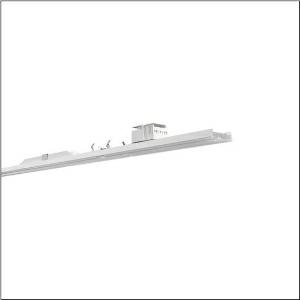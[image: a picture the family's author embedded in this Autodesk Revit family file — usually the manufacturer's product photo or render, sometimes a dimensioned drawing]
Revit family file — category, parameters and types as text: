
# Revit family: licross_r__11_recessed_extreme_mo_51tl11dn49xfe_ba7a
name_source: partatom
category: Lighting Fixtures
units: mm (PartAtom-declared; Revit-internal decimal feet)

## family parameters
Cut with Voids When Loaded = No
Host = Face
Light Source = No
Part Type = Normal
Room Calculation Point = No
Round Connector Dimension = Use Diameter
Shared = No

## types (1)
- --- (1 x LED, 9030 lm, 55.4 W, 4000K)
    Apparent Load = 55 VA
    CIE Flux Codes = 89 96 99 100 100
    Color Rendering = 80
    Color Temperature = 4000K
    Default Elevation = 1800 mm
    Description = Licross® 11 Recessed extreme MOluminaire insert, length: 1.500mm, width: 66mm, height: 67mm, LED rated luminous flux: 9.030lm, light colour: 840, control gear: DALI 2, control gear: ECG DALI, with plug, 5-pole, with phase selection, mains connection: 220..240V, AC, 50/60Hz, halogen-free wiring, primary optical cover: cover, of PMMA, light emission: direct distribution, protection rating (complete): IP40, insulation class (complete): insulation class I (protective earthing), certification: CE, ENEC, VDE, protection symbol: D if used in an environment without relevant dust loads with corresponding accessories, permissible ambient temperature for indoor applications: -25..+50°C, reducing of maximum allowable ambient temperature of 5°C with ceiling mounting, corresponds to IFS (International Featured Standards) requirements for safety and quality in the food industry, packaging unit: 1 piece
    Height = 58 mm
    Lamp = 1 x LED
    Lamp Light Flux = 9030 lm
    Lamp Power = 55.4 W
    Lamp count = 1
    Length = 1500 mm
    Luminous efficacy = 163 lm/W
    Manufacturer = Siteco
    ModVariant = No
    Model = 51TL11DN49XFE
    Mounting Place = Ceiling
    Mounting Type = Pendant
    Number of Poles = 1
    OnlyDefault = Yes
    Power Factor = 1
    Product Name = Licross® 11 Recessed extreme MO
    Product group = luminaire insert
    ProductGroupID = 902
    Protection Class = Protection class I
    Protection Degree = IP 40
    RLX_Detail_Level = 1
    RlxData = <blob elided: 22165 chars, md5=d3ffa249>
    Socket = socket
    Standby Power = 0 W
    System Light Flux = 9030 lm
    System Power = 55 W
    Type Comments = factory setting: luminous flux: 100 % | dim-lin: 254 | 365 mA
    Type Image = l_1266722.jpg
    URL = http://relux.com
    VarID = @adj_132434
    Voltage = 0 V
    Weight = 0.00 kg
    Width = 66 mm

## geometry (parser evidence)
native form markers: Blend x4, Sweep x11
no freeform markers — native parametric forms only
